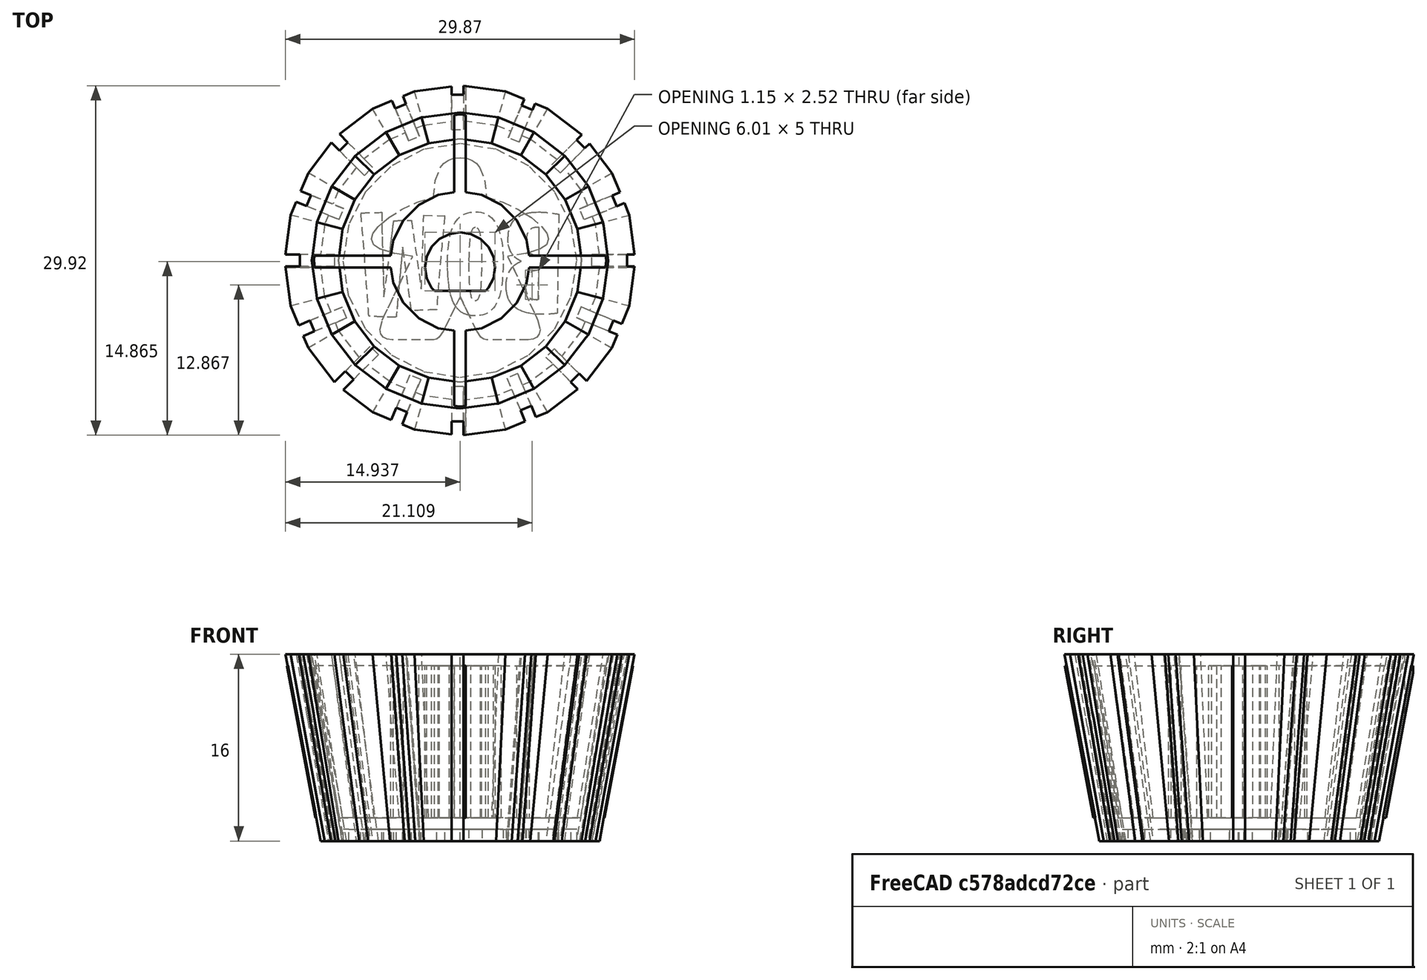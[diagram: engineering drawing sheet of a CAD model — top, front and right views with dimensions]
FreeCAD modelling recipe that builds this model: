
FCSTD DOCUMENT  (FreeCAD 0.17R13522 (Git))
Label: stove_knob
License: All rights reserved
LicenseURL: http://en.wikipedia.org/wiki/All_rights_reserved
objects: Part::Feature×3, Mesh::Feature×1, Part::Cylinder×1, Part::Cut×1, Part::Part2DObjectPython×1, Part::Mirroring×1, Part::Extrusion×1, Part::MultiFuse×1
note: 9 computed .brp shape members not serialized (recipe doc carries the construction recipe); baked Part::Feature solids carry a one-line shape summary decoded from their .brp

FEATURE [Mesh::Feature] Camp_Stove_Knob
FEATURE [Part::Cylinder] Cylinder
  Angle = 360
  AttacherType = Attacher::AttachEngine3D
  Height = 1
  Placement = pos=(6,7,0) rot=(0,0,1;0rad)
  Radius = 9.8
FEATURE [Part::Feature] Camp_Stove_Knob001
  shape: bbox 29.87 x 29.92 x 16 mm, 1254 faces, 0 solids (baked)
FEATURE [Part::Feature] Camp_Stove_Knob001001  label="Camp_Stove_Knob002"
  shape: bbox 29.87 x 29.92 x 16 mm, 541 faces, 0 solids (baked)
FEATURE [Part::Feature] Camp_Stove_Knob001001_solid  label="Camp_Stove_Knob002 (Solid)"
  shape: bbox 29.87 x 29.92 x 16 mm, 541 faces (baked)
FEATURE [Part::Cut] Cut
  Base = -> Camp_Stove_Knob001001_solid
  Tool = -> Cylinder
FEATURE [Part::Part2DObjectPython] ShapeString  # Draft 2D object (typed FeaturePython)
  FontFile = <userpath>/Downloads/BurbankBigCondensed-Bold.otf
  Placement = pos=(-0.233478,24.48,0) rot=(0,0,1;0rad)
  Size = 4
  String = BOW
  Tracking = 0
FEATURE [Part::Mirroring] mirror  label="Mirror of ShapeString"
  Base = (0,0,0)
  Normal = (-0.999999,0.00140638,0)
  Source = -> ShapeString
FEATURE [Part::Extrusion] Extrude
  Base = -> mirror
  Dir = (0,0,1)
  DirMode = 0
  FaceMakerClass = Part::FaceMakerBullseye
  LengthFwd = 1
  LengthRev = 0
  Placement = pos=(14.5,-22,0) rot=(0,0,1;0rad)
  Solid = false
  Symmetric = false
FEATURE [Part::MultiFuse] Fusion
  Shapes = -> [Cut,Extrude]
